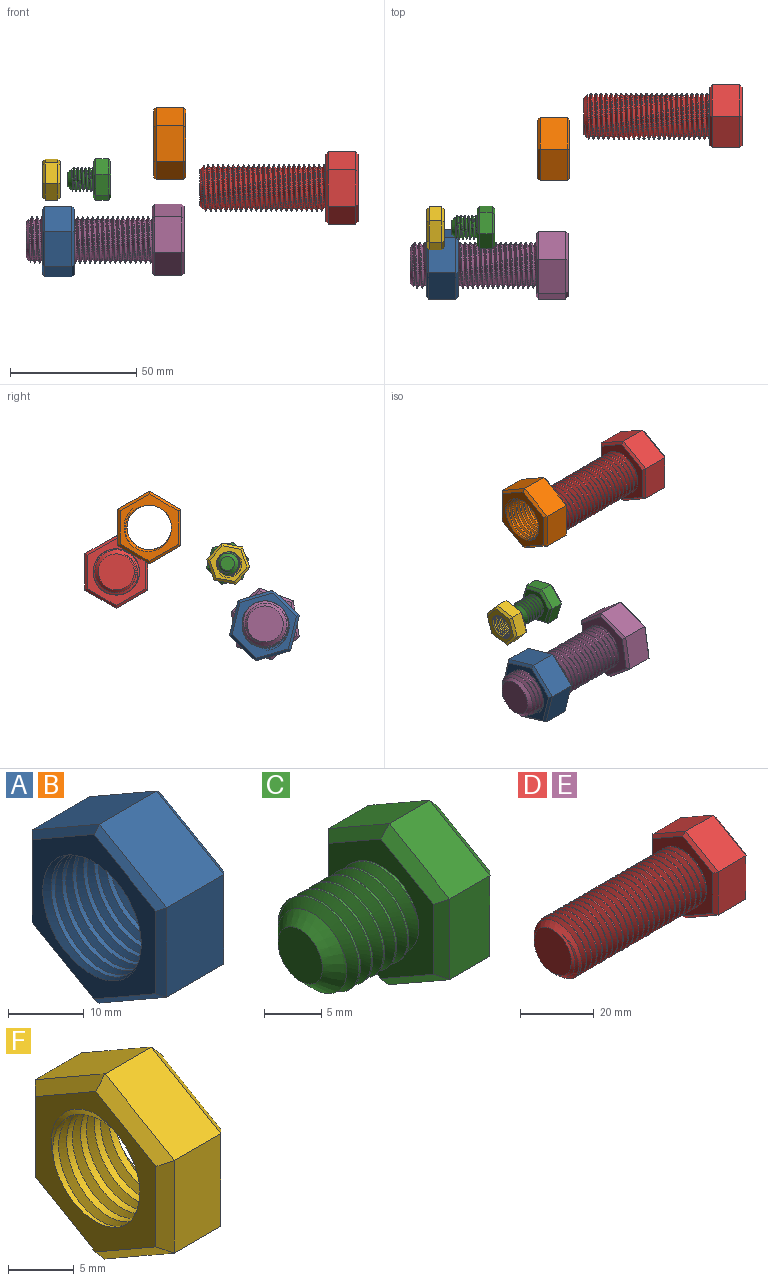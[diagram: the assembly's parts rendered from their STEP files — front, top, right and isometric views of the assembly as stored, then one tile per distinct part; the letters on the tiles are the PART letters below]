
ASSEMBLY  parts=6 mates=2
PART A: 23 faces, bbox 15x25.7x29.6 mm
  f0: cylinder r=8.82mm len=17.65mm, axis (1,0,0), area 227.8mm2, adj f7,f8,f21,f22
  f1: plane 12.48x10.7mm, normal (0,-0.5,0.86), area 154.4mm2, adj f2,f6,f14,f18
  f2: plane 14.43x10.7mm, normal (0,-1,0), area 154.4mm2, adj f1,f3,f12,f16
  f3: plane 12.52x10.7mm, normal (0,-0.5,-0.87), area 154.4mm2, adj f2,f4,f10,f15
  f4: plane 12.48x10.7mm, normal (0,0.5,-0.86), area 154.4mm2, adj f3,f5,f9,f17
  f5: plane 14.43x10.7mm, normal (0,1,0), area 154.4mm2, adj f4,f6,f11,f19
  f6: plane 12.52x10.7mm, normal (0,0.5,0.87), area 154.4mm2, adj f1,f5,f13,f20
  f7: plane 27.21x23.69mm, normal (-1,0,0), area 192.4mm2, adj f0,f9,f10,f11,f12,f13,f14,f21
  f8: plane 27.25x23.72mm, normal (1,0,0), area 192.4mm2, adj f0,f15,f16,f17,f18,f19,f20,f21
  f9: plane 12.48x7.82mm, normal (-0.71,0.36,-0.61), area 19.6mm2, adj f4,f7,f10,f11
  f10: plane 12.52x7.77mm, normal (-0.71,-0.35,-0.61), area 19.6mm2, adj f3,f7,f9,f12
  f11: plane 14.43x1.04mm, normal (-0.71,0.71,0), area 19.6mm2, adj f5,f7,f9,f13
  f12: plane 14.43x1.04mm, normal (-0.71,-0.71,0), area 19.6mm2, adj f2,f7,f10,f14
  f13: plane 12.52x7.77mm, normal (-0.71,0.35,0.61), area 19.6mm2, adj f6,f7,f11,f14
  f14: plane 12.48x7.82mm, normal (-0.71,-0.36,0.61), area 19.6mm2, adj f1,f7,f12,f13
  f15: plane 12.52x7.77mm, normal (0.71,-0.35,-0.61), area 19.6mm2, adj f3,f8,f16,f17
  f16: plane 14.43x1.04mm, normal (0.71,-0.71,0), area 19.6mm2, adj f2,f8,f15,f18
  f17: plane 12.48x7.82mm, normal (0.71,0.36,-0.61), area 19.6mm2, adj f4,f8,f15,f19
  f18: plane 12.48x7.82mm, normal (0.71,-0.36,0.61), area 19.6mm2, adj f1,f8,f16,f20
  f19: plane 14.43x1.04mm, normal (0.71,0.71,0), area 19.6mm2, adj f5,f8,f17,f20
  f20: plane 12.52x7.77mm, normal (0.71,0.35,0.61), area 19.6mm2, adj f6,f8,f18,f19
  f21: bspline ~22.98x19.9mm, area 486.2mm2, adj f0,f7,f8,f22
  f22: bspline ~22.98x19.9mm, area 485.7mm2, adj f0,f7,f8,f21
PART B: same geometry as A
PART C: 25 faces, bbox 17.8x15.9x18.1 mm
  f0: cylinder r=4.75mm len=9.5mm, axis (1,0,0), area 28.1mm2, adj f1,f2,f4,f12
  f1: bspline ~10.97x9.91mm, area 196.7mm2, adj f0,f2,f4,f12
  f2: bspline ~10.97x10.66mm, area 196.6mm2, adj f0,f1,f4,f12
  f3: plane 5.5x5.5mm, normal (-1,0,0), area 23.8mm2, adj f4
  f4: cone r=4.75mm half-angle=45deg, axis (1,0,0), area 47.4mm2, adj f0,f1,f2,f3
  f5: plane 7.48x5mm, normal (0,-0.5,0.86), area 43.3mm2, adj f6,f10,f18,f22
  f6: plane 8.66x5mm, normal (0,-1,0), area 43.3mm2, adj f5,f7,f16,f20
  f7: plane 7.52x5mm, normal (0,-0.5,-0.87), area 43.3mm2, adj f6,f8,f14,f19
  f8: plane 7.48x5mm, normal (0,0.5,-0.86), area 43.3mm2, adj f7,f9,f13,f21
  f9: plane 8.66x5mm, normal (0,1,0), area 43.3mm2, adj f8,f10,f15,f23
  f10: plane 7.52x5mm, normal (0,0.5,0.87), area 43.3mm2, adj f5,f9,f17,f24
  f11: plane 15.01x13.03mm, normal (1,0,0), area 146.4mm2, adj f13,f14,f15,f16,f17,f18
  f12: plane 15.83x13.85mm, normal (-1,0,0), area 89.2mm2, adj f0,f1,f2,f19,f20,f21,f22,f23
  f13: plane 7.49x4.93mm, normal (0.71,0.36,-0.61), area 11.4mm2, adj f8,f11,f14,f15
  f14: plane 7.52x4.88mm, normal (0.71,-0.35,-0.61), area 11.4mm2, adj f7,f11,f13,f16
  f15: plane 8.66x1.03mm, normal (0.71,0.71,0), area 11.4mm2, adj f9,f11,f13,f17
  f16: plane 8.66x1.03mm, normal (0.71,-0.71,0), area 11.4mm2, adj f6,f11,f14,f18
  f17: plane 7.52x4.88mm, normal (0.71,0.35,0.61), area 11.4mm2, adj f10,f11,f15,f18
  f18: plane 7.49x4.93mm, normal (0.71,-0.36,0.61), area 11.4mm2, adj f5,f11,f16,f17
  f19: plane 7.52x4.88mm, normal (-0.71,-0.35,-0.61), area 11.4mm2, adj f7,f12,f20,f21
  f20: plane 8.66x1.03mm, normal (-0.71,-0.71,0), area 11.4mm2, adj f6,f12,f19,f22
  f21: plane 7.49x4.93mm, normal (-0.71,0.36,-0.61), area 11.4mm2, adj f8,f12,f19,f23
  f22: plane 7.49x4.93mm, normal (-0.71,-0.36,0.61), area 11.4mm2, adj f5,f12,f20,f24
  f23: plane 8.66x1.03mm, normal (-0.71,0.71,0), area 11.4mm2, adj f9,f12,f21,f24
  f24: plane 7.52x4.88mm, normal (-0.71,0.35,0.61), area 11.4mm2, adj f10,f12,f22,f23
PART D: 30 faces, bbox 64.4x26.2x30 mm
  f0: cylinder r=9.14mm len=48mm, axis (1,0,0), area 814.9mm2, adj f1,f2,f4,f12
  f1: bspline ~50.54x21.12mm, area 2246.8mm2, adj f0,f2,f4,f12
  f2: bspline ~51.54x21.12mm, area 2245.6mm2, adj f0,f1,f4,f12
  f3: plane 14.29x14.29mm, normal (-1,0,0), area 160.3mm2, adj f4
  f4: cone r=9.14mm half-angle=45deg, axis (1,0,0), area 93.9mm2, adj f0,f1,f2,f3
  f5: plane 12.48x10.7mm, normal (0,-0.5,0.86), area 154.4mm2, adj f6,f10,f18,f22
  f6: plane 14.43x10.7mm, normal (0,-1,0), area 154.4mm2, adj f5,f7,f16,f20
  f7: plane 12.52x10.7mm, normal (0,-0.5,-0.87), area 154.4mm2, adj f6,f8,f14,f19
  f8: plane 12.48x10.7mm, normal (0,0.5,-0.86), area 154.4mm2, adj f7,f9,f13,f21
  f9: plane 14.43x10.7mm, normal (0,1,0), area 154.4mm2, adj f8,f10,f15,f23
  f10: plane 12.52x10.7mm, normal (0,0.5,0.87), area 154.4mm2, adj f5,f9,f17,f24
  f11: plane 26.56x23.04mm, normal (1,0,0), area 397.6mm2, adj f13,f14,f15,f16,f17,f18,f25,f26
  f12: plane 27.71x24.2mm, normal (-1,0,0), area 231.5mm2, adj f0,f1,f2,f19,f20,f21,f22,f23
  f13: plane 12.48x7.83mm, normal (0.71,0.36,-0.61), area 19.6mm2, adj f8,f11,f14,f15
  f14: plane 12.52x7.76mm, normal (0.71,-0.35,-0.61), area 19.6mm2, adj f7,f11,f13,f16
  f15: plane 14.43x1.04mm, normal (0.71,0.71,0), area 19.6mm2, adj f9,f11,f13,f17
  f16: plane 14.43x1.04mm, normal (0.71,-0.71,0), area 19.6mm2, adj f6,f11,f14,f18
  f17: plane 12.52x7.76mm, normal (0.71,0.35,0.61), area 19.6mm2, adj f10,f11,f15,f18
  f18: plane 12.48x7.83mm, normal (0.71,-0.36,0.61), area 19.6mm2, adj f5,f11,f16,f17
  f19: plane 12.52x7.76mm, normal (-0.71,-0.35,-0.61), area 19.6mm2, adj f7,f12,f20,f21
  f20: plane 14.43x1.04mm, normal (-0.71,-0.71,0), area 19.6mm2, adj f6,f12,f19,f22
  f21: plane 12.48x7.83mm, normal (-0.71,0.36,-0.61), area 19.6mm2, adj f8,f12,f19,f23
  f22: plane 12.48x7.83mm, normal (-0.71,-0.36,0.61), area 19.6mm2, adj f5,f12,f20,f24
  f23: plane 14.43x1.04mm, normal (-0.71,0.71,0), area 19.6mm2, adj f9,f12,f21,f24
  f24: plane 12.52x7.76mm, normal (-0.71,0.35,0.61), area 19.6mm2, adj f10,f12,f22,f23
  f25: plane 5x3.18mm, normal (0,1,0), area 15.9mm2, adj f11,f26,f28,f29
  f26: plane 19.05x5mm, normal (0,0,1), area 95.2mm2, adj f11,f25,f27,f29
  f27: plane 5x3.18mm, normal (0,-1,0), area 15.9mm2, adj f11,f26,f28,f29
  f28: plane 19.05x5mm, normal (0,0,-1), area 95.2mm2, adj f11,f25,f27,f29
  f29: plane 19.05x3.18mm, normal (1,0,0), area 60.5mm2, adj f25,f26,f27,f28
PART E: same geometry as D
PART F: 23 faces, bbox 9.1x15.4x17.7 mm
  f0: plane 7.49x5mm, normal (0,-0.5,0.86), area 43.3mm2, adj f1,f5,f13,f17
  f1: plane 8.66x5mm, normal (0,-1,0), area 43.3mm2, adj f0,f2,f11,f15
  f2: plane 7.51x5mm, normal (0,-0.5,-0.87), area 43.3mm2, adj f1,f3,f9,f14
  f3: plane 7.49x5mm, normal (0,0.5,-0.86), area 43.3mm2, adj f2,f4,f8,f16
  f4: plane 8.66x5mm, normal (0,1,0), area 43.3mm2, adj f3,f5,f10,f18
  f5: plane 7.51x5mm, normal (0,0.5,0.87), area 43.3mm2, adj f0,f4,f12,f19
  f6: plane 15.37x13.38mm, normal (-1,0,0), area 71.4mm2, adj f8,f9,f10,f11,f12,f13,f20,f21
  f7: plane 15.37x13.38mm, normal (1,0,0), area 71.4mm2, adj f14,f15,f16,f17,f18,f19,f20,f21
  f8: plane 7.49x4.93mm, normal (-0.71,0.36,-0.61), area 11.4mm2, adj f3,f6,f9,f10
  f9: plane 7.51x4.89mm, normal (-0.71,-0.35,-0.61), area 11.4mm2, adj f2,f6,f8,f11
  f10: plane 8.66x1.02mm, normal (-0.71,0.71,0), area 11.4mm2, adj f4,f6,f8,f12
  f11: plane 8.66x1.02mm, normal (-0.71,-0.71,0), area 11.4mm2, adj f1,f6,f9,f13
  f12: plane 7.51x4.89mm, normal (-0.71,0.35,0.61), area 11.4mm2, adj f5,f6,f10,f13
  f13: plane 7.49x4.93mm, normal (-0.71,-0.36,0.61), area 11.4mm2, adj f0,f6,f11,f12
  f14: plane 7.51x4.89mm, normal (0.71,-0.35,-0.61), area 11.4mm2, adj f2,f7,f15,f16
  f15: plane 8.66x1.02mm, normal (0.71,-0.71,0), area 11.4mm2, adj f1,f7,f14,f17
  f16: plane 7.49x4.93mm, normal (0.71,0.36,-0.61), area 11.4mm2, adj f3,f7,f14,f18
  f17: plane 7.49x4.93mm, normal (0.71,-0.36,0.61), area 11.4mm2, adj f0,f7,f15,f19
  f18: plane 8.66x1.02mm, normal (0.71,0.71,0), area 11.4mm2, adj f4,f7,f16,f19
  f19: plane 7.51x4.89mm, normal (0.71,0.35,0.61), area 11.4mm2, adj f5,f7,f17,f18
  f20: cylinder r=4.66mm len=9.32mm, axis (1,0,0), area 85.4mm2, adj f6,f7,f21,f22
  f21: bspline ~12.5x10.82mm, area 128.4mm2, adj f6,f7,f20,f22
  f22: bspline ~12.5x10.82mm, area 128.5mm2, adj f6,f7,f20,f21
PLACE A rot(axis=(0,0.6,-0.8),180deg) t=(-55.27,-6.86,23.48)mm fixed
PLACE B t=(1.48,38.75,62.34)mm
PLACE C rot(axis=(-1,0,0),43.8deg) t=(-31.66,7.73,48.08)mm
PLACE D t=(63.44,51.78,44.72)mm
PLACE E rot(axis=(1,0,0),170.4deg) t=(-5.42,-7.2,24.11)mm
PLACE F rot(axis=(1,0,0),100.2deg) t=(-48.16,7.38,48.02)mm fixed
MATE cylindrical E.f0 <-> A.f7  axis (-1,0,0) through (-61.77,-7.2,24.11)mm
MATE cylindrical C.f0 <-> F.f6  axis (-1,0,0) through (-45.16,7.73,48.08)mm
